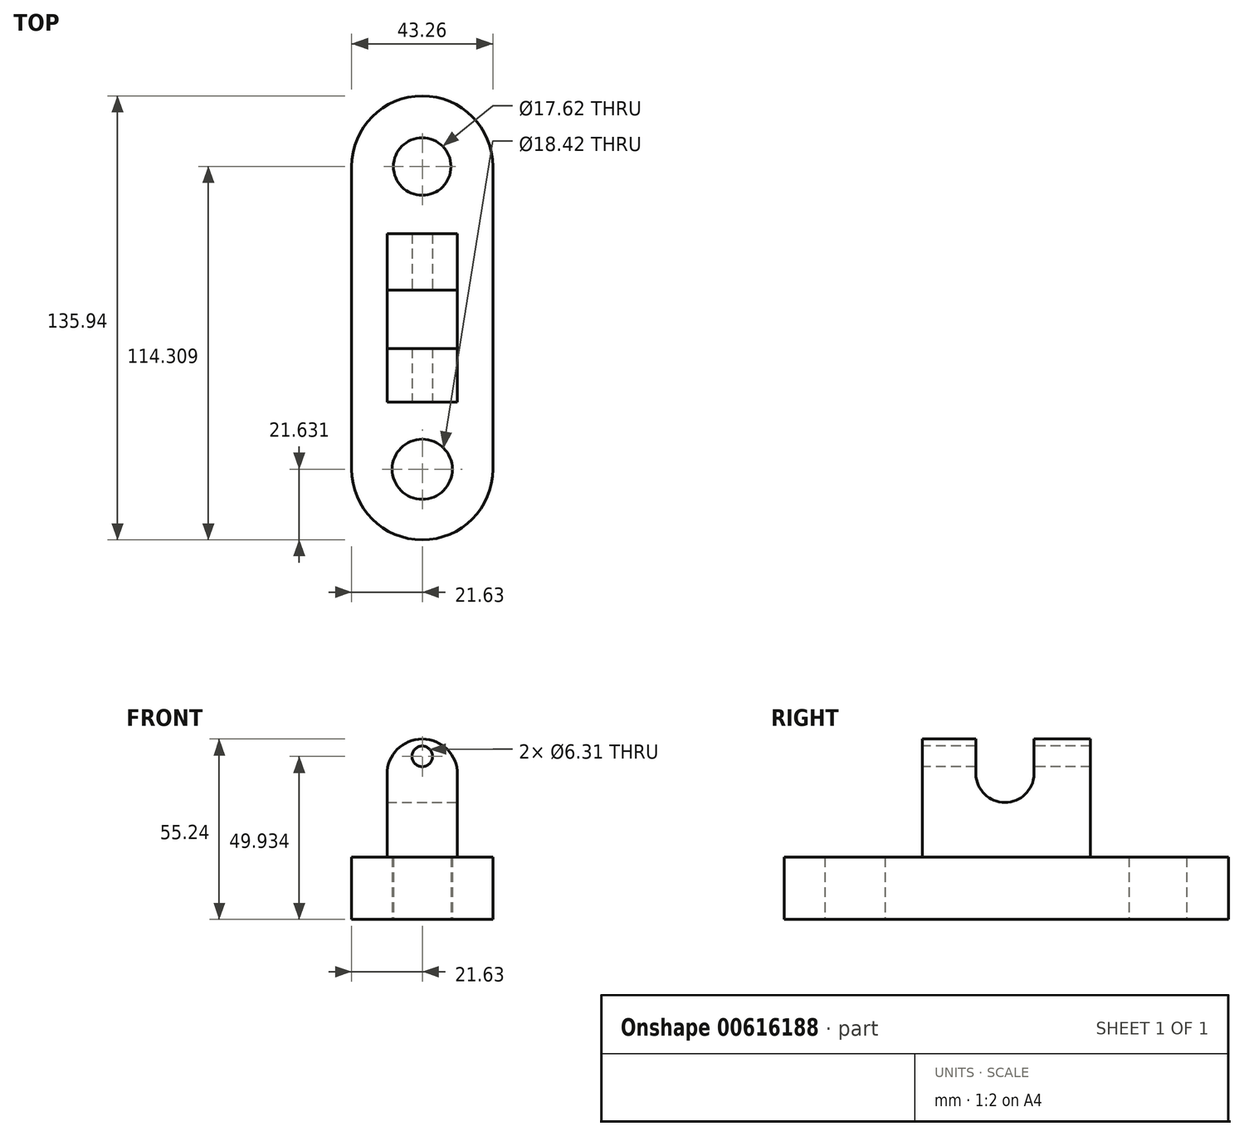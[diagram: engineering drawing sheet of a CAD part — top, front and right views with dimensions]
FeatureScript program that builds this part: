
annotation { "Feature Type Name" : "Feature", "Feature Type Description" : "" }
export const myFeature = defineFeature(function(context is Context, id is Id, definition is map)
    precondition{}
    {
        {
            var Q0;
            Q0=qCreatedBy(makeId("Top.planeOp"),FACE);
            var sketch = newSketch(context, id + "F0", { "sketchPlane" : qUnion([Q0])});
            skLineSegment(sketch, "E0.left", {"start": v(-21.63, 46.34) * mm, "end": v(-21.63, -46.34) * mm});
            skLineSegment(sketch, "E0.right", {"start": v(21.63, 46.34) * mm, "end": v(21.63, -46.34) * mm});
            skPoint(sketch, "E0.middle", {"position": v(0, 0) * mm});
            skArc(sketch, "E1", {"start": v(-21.63, -46.34) * mm, "mid": v(0, -67.97) * mm, "end": v(21.63, -46.34) * mm});
            skArc(sketch, "E2", {"start": v(21.63, 46.34) * mm, "mid": v(0, 67.97) * mm, "end": v(-21.63, 46.34) * mm});
            skCircle(sketch, "E3", {"center": v(0, 46.34) * mm, "radius": 8.8 * mm});
            skCircle(sketch, "E4", {"center": v(0, -46.34) * mm, "radius": 9.2 * mm});
            skSolve(sketch);
        }
        {
            var Q0;
            Q0 = qSketchRegion(id + "F0", true);
            extrude(context, id + "F1", {"entities" : qUnion([Q0]), "depth" : 19.05 * mm, "offsetDistance" : 25.4 * mm});
        }
        {
            var Q0;
            Q0=makeQuery(id+"F1.opExtrude","CAP_FACE",FACE,{"disambiguationData":[OSD([sQuery(id+"F0.wireOp",EDGE,"E0.left"),sQuery(id+"F0.wireOp",EDGE,"E0.right"),sQuery(id+"F0.wireOp",EDGE,"E1"),sQuery(id+"F0.wireOp",EDGE,"E2"),sQuery(id+"F0.wireOp",EDGE,"E3"),sQuery(id+"F0.wireOp",EDGE,"E4")])],"isStart":false});
            var sketch = newSketch(context, id + "F2", { "sketchPlane" : qUnion([Q0])});
            skLineSegment(sketch, "E5.bottom", {"start": v(-10.8, 25.76) * mm, "end": v(10.8, 25.76) * mm});
            skLineSegment(sketch, "E5.top", {"start": v(-10.8, -25.76) * mm, "end": v(10.8, -25.76) * mm});
            skLineSegment(sketch, "E5.left", {"start": v(-10.8, 25.76) * mm, "end": v(-10.8, -25.76) * mm});
            skLineSegment(sketch, "E5.right", {"start": v(10.8, 25.76) * mm, "end": v(10.8, -25.76) * mm});
            skPoint(sketch, "E5.middle", {"position": v(0, 0) * mm});
            skSolve(sketch);
        }
        {
            var Q0;
            Q0 = qSketchRegion(id + "F2", true);
            extrude(context, id + "F3", {"entities" : qUnion([Q0]), "operationType" : NewBodyOperationType.ADD, "depth" : 25.4 * mm, "offsetDistance" : 25.4 * mm});
        }
        {
            var Q0;
            Q0=makeQuery(id+"F3.opExtrude","SWEPT_FACE",FACE,{"disambiguationData":[OSD([sQuery(id+"F2.wireOp",EDGE,"E5.top")])]});
            var sketch = newSketch(context, id + "F4", { "sketchPlane" : qUnion([Q0])});
            skArc(sketch, "E6", {"start": v(10.8, 44.45) * mm, "mid": v(0, 55.24) * mm, "end": v(-10.8, 44.45) * mm});
            skLineSegment(sketch, "E7", {"start": v(0, 44.45) * mm, "end": v(10.8, 44.45) * mm});
            skLineSegment(sketch, "E8", {"start": v(0, 44.45) * mm, "end": v(-10.8, 44.45) * mm});
            skSolve(sketch);
        }
        {
            var Q0;
            Q0 = qSketchRegion(id + "F4", true);
            extrude(context, id + "F5", {"entities" : qUnion([Q0]), "operationType" : NewBodyOperationType.ADD, "depth" : -53.34 * mm, "offsetDistance" : 25.4 * mm});
        }
        {
            var Q0;
            Q0=qCreatedBy(makeId("Right.planeOp"),FACE);
            var sketch = newSketch(context, id + "F6", { "sketchPlane" : qUnion([Q0])});
            skLineSegment(sketch, "E9", {"start": v(25.76, 44.75) * mm, "end": v(25.76, 59.14) * mm});
            skLineSegment(sketch, "E10", {"start": v(25.76, 59.14) * mm, "end": v(39.57, 59.14) * mm});
            skLineSegment(sketch, "E11", {"start": v(39.57, 59.14) * mm, "end": v(39.57, 35.54) * mm});
            skLineSegment(sketch, "E12", {"start": v(40.44, 35.54) * mm, "end": v(25.76, 35.54) * mm});
            skLineSegment(sketch, "E13", {"start": v(25.76, 35.54) * mm, "end": v(25.76, 44.75) * mm});
            skSolve(sketch);
        }
        {
            var Q0;
            Q0=makeQuery(id+"F6.imprint","IMPRINT",FACE,{"disambiguationData":[TD([[makeQuery(id+"F6.imprint","IMPRINT",EDGE,{"derivedFrom":sQuery(id+"F6.wireOp",EDGE,"E9")}),-1.0]])]});
            extrude(context, id + "F7", {"entities" : qUnion([Q0]), "operationType" : NewBodyOperationType.REMOVE, "oppositeDirection" : true, "depth" : 25.4 * mm, "offsetDistance" : 25.4 * mm});
        }
        {
            var Q0;
            Q0 = qSketchRegion(id + "F6", true);
            extrude(context, id + "F8", {"entities" : qUnion([Q0]), "operationType" : NewBodyOperationType.REMOVE, "oppositeDirection" : true, "depth" : -25.4 * mm, "offsetDistance" : 25.4 * mm});
        }
        {
            var Q0;
            Q0=qCreatedBy(makeId("Right.planeOp"),FACE);
            var sketch = newSketch(context, id + "F9", { "sketchPlane" : qUnion([Q0])});
            skLineSegment(sketch, "E14.bottom", {"start": v(-9.35, 44.75) * mm, "end": v(8.5, 44.75) * mm});
            skLineSegment(sketch, "E14.top", {"start": v(-9.35, 69.8) * mm, "end": v(8.5, 69.8) * mm});
            skLineSegment(sketch, "E14.left", {"start": v(-9.35, 44.75) * mm, "end": v(-9.35, 69.8) * mm});
            skLineSegment(sketch, "E14.right", {"start": v(8.5, 44.75) * mm, "end": v(8.5, 69.8) * mm});
            skArc(sketch, "E15", {"start": v(-9.35, 44.75) * mm, "mid": v(-0.43, 35.83) * mm, "end": v(8.5, 44.75) * mm});
            skSolve(sketch);
        }
        {
            var Q0;
            Q0 = qSketchRegion(id + "F9", true);
            extrude(context, id + "F10", {"entities" : qUnion([Q0]), "operationType" : NewBodyOperationType.REMOVE, "oppositeDirection" : true, "depth" : 25.4 * mm, "offsetDistance" : 25.4 * mm});
        }
        {
            var Q0;
            Q0 = qSketchRegion(id + "F9", true);
            extrude(context, id + "F11", {"entities" : qUnion([Q0]), "operationType" : NewBodyOperationType.REMOVE, "oppositeDirection" : true, "depth" : -25.4 * mm, "offsetDistance" : 25.4 * mm});
        }
        {
            var Q0;
            Q0=makeQuery(id+"F5.boolean.opBoolean","MERGE",FACE,{"derivedFrom":[makeQuery(id+"F3.opExtrude","SWEPT_FACE",FACE,{"disambiguationData":[OSD([sQuery(id+"F2.wireOp",EDGE,"E5.top")])]}),makeQuery(id+"F5.opExtrude","CAP_FACE",FACE,{"disambiguationData":[OSD([sQuery(id+"F4.wireOp",EDGE,"E6"),sQuery(id+"F4.wireOp",EDGE,"E7"),sQuery(id+"F4.wireOp",EDGE,"E8")])],"isStart":true})]});
            var sketch = newSketch(context, id + "F12", { "sketchPlane" : qUnion([Q0])});
            skCircle(sketch, "E16", {"center": v(0, 49.93) * mm, "radius": 3.16 * mm});
            skPoint(sketch, "E16.centerSnap0", {"position": v(0, 55.24) * mm});
            skSolve(sketch);
        }
        {
            var Q0;
            Q0=makeQuery(id+"F12.imprint","IMPRINT",FACE,{"disambiguationData":[TD([[makeQuery(id+"F12.imprint","IMPRINT",EDGE,{"derivedFrom":sQuery(id+"F12.wireOp",EDGE,"E16")}),1.0]])]});
            extrude(context, id + "F13", {"entities" : qUnion([Q0]), "operationType" : NewBodyOperationType.REMOVE, "oppositeDirection" : true, "depth" : 76.2 * mm, "offsetDistance" : 25.4 * mm});
        }
    });
